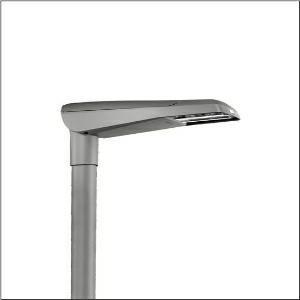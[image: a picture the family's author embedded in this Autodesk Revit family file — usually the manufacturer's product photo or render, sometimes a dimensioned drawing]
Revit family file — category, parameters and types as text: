
# Revit family: streetlight_sl_11_iq_micro___p1_0a_5xc1c41f08ce_dca2
name_source: partatom
category: Lighting Fixtures
units: mm (PartAtom-declared; Revit-internal decimal feet)

## family parameters
Cut with Voids When Loaded = No
Host = Face
Light Source = No
Part Type = Normal
Room Calculation Point = No
Round Connector Dimension = Use Diameter
Shared = No

## types (1)
- --- (1 x LED, 1660 lm, 10.8 W, 4000K)
    Apparent Load = 11 VA
    CIE Flux Codes = 29 63 93 100 100
    Color Rendering = 70
    Color Temperature = 4000K
    Default Elevation = 1800 mm
    Description = Streetlight SL 11 iQ micro, mast luminaire, primary light control with 3 zone facetted reflector, of plastic, silver coated, highly specular, primary optical cover: cover, of PMMA, transparent, light distribution: P1.0a, light emission: direct distribution, primary light characteristic: asymmetric, installation type: post-top, side-entry, lamps: LED, High Power LED, rated values: 1.660lm | 10,8W | 153,7lm/W (begin service life); end service life: 1.660lm | 11,1W; at 50% lumin. flux: 830lm | 6W | 138,3lm/W, colour temperature: 4000K, colour rendering: CRI > 70, light colour: 740, light setting 1 begin service life: 100% | 1.660lm | 10,8W | 153,7lm/W | 4.000K, light setting 1 end service life: 11,1W, further light settings possible, control: Street-Remote, optimised constant luminous flux control (CLO 2.0), Desk-Remote (wireless, voltage-free reading and setting of iQ features in the workshop via application-optimized NFC function/RFID function), Light-Fading, Smart-Wire, Night-Set, Lumen-Switch, Temp-Guard, Auto-Match, with cable H07RN-F 5x 1.5mm², mains connection: 230..240V, AC, 50/60Hz, connection cable pre-assembled, cable length: 5,5m, luminaire housing, of diecast aluminium, powder-coated, Siteco® metallic grey (DB 702S), please order mast flange separately, inclination adjustable without tools: 0°, 5°, 10°, 15° (post-top) | 0°, -5°, -10°, -15° (side-entry), sealing non-destructively replaceable, multi-level sealing system, length: 600mm, width: 174mm, height: 116mm, mast flange for spigot size: 42mm (side-entry): 5XC10008XM4, 60/48mm (side-entry/post-top): 5XC10108XM2, 76/60mm (side-entry/post-top): 5XC10108XM1, equipment: standard, protection rating (complete): IP66, insulation class (complete): insulation class II (safety insulation), certification: CE, ENEC, ENEC+, VDE, impact resistance: IK10, permissible operating ambient temperature for outdoor applications: -25..+50°C, standard-compliant lighting for roads and squares, Environmental Product Declaration (EPD) tested and certified by an independent institute, packaging unit: 1 piece

Light Distribution: P1.0a
    Height = 116 mm
    Lamp = 1 x LED
    Lamp Light Flux = 1660 lm
    Lamp Power = 10.8 W
    Lamp count = 1
    Length = 600 mm
    Luminous efficacy = 154 lm/W
    Manufacturer = Siteco
    ModVariant = No
    Model = 5XC1C41F08CE
    Number of Poles = 1
    OnlyDefault = Yes
    Power Factor = 1
    Product Name = Streetlight SL 11 iQ micro | P1.0a
    Product group = mast luminaire | pylon top
    ProductGroupID = 6100
    Protection Class = Protection class II
    Protection Degree = IP 66
    RLX_Detail_Level = 1
    RLX_Emergency_Light_Flux = 0 lm
    RLX_Emergency_Type = 0
    RLX_Emergency_Type_DB = No
    RlxData = <blob elided: 26621 chars, md5=47c29d51>
    Socket = socket
    Standby Power = 0 W
    System Light Flux = 1660 lm
    System Power = 11 W
    Type Comments = factory setting: luminous flux: 100 % | dim-lin: 254 | 194 mA
    Type Image = l_1006566.jpg
    URL = http://relux.com
    VarID = @adj_001159
    Voltage = 0 V
    Weight = 0.00 kg
    Width = 174 mm

## geometry (parser evidence)
native form markers: Blend x4, Sweep x11
no freeform markers — native parametric forms only
